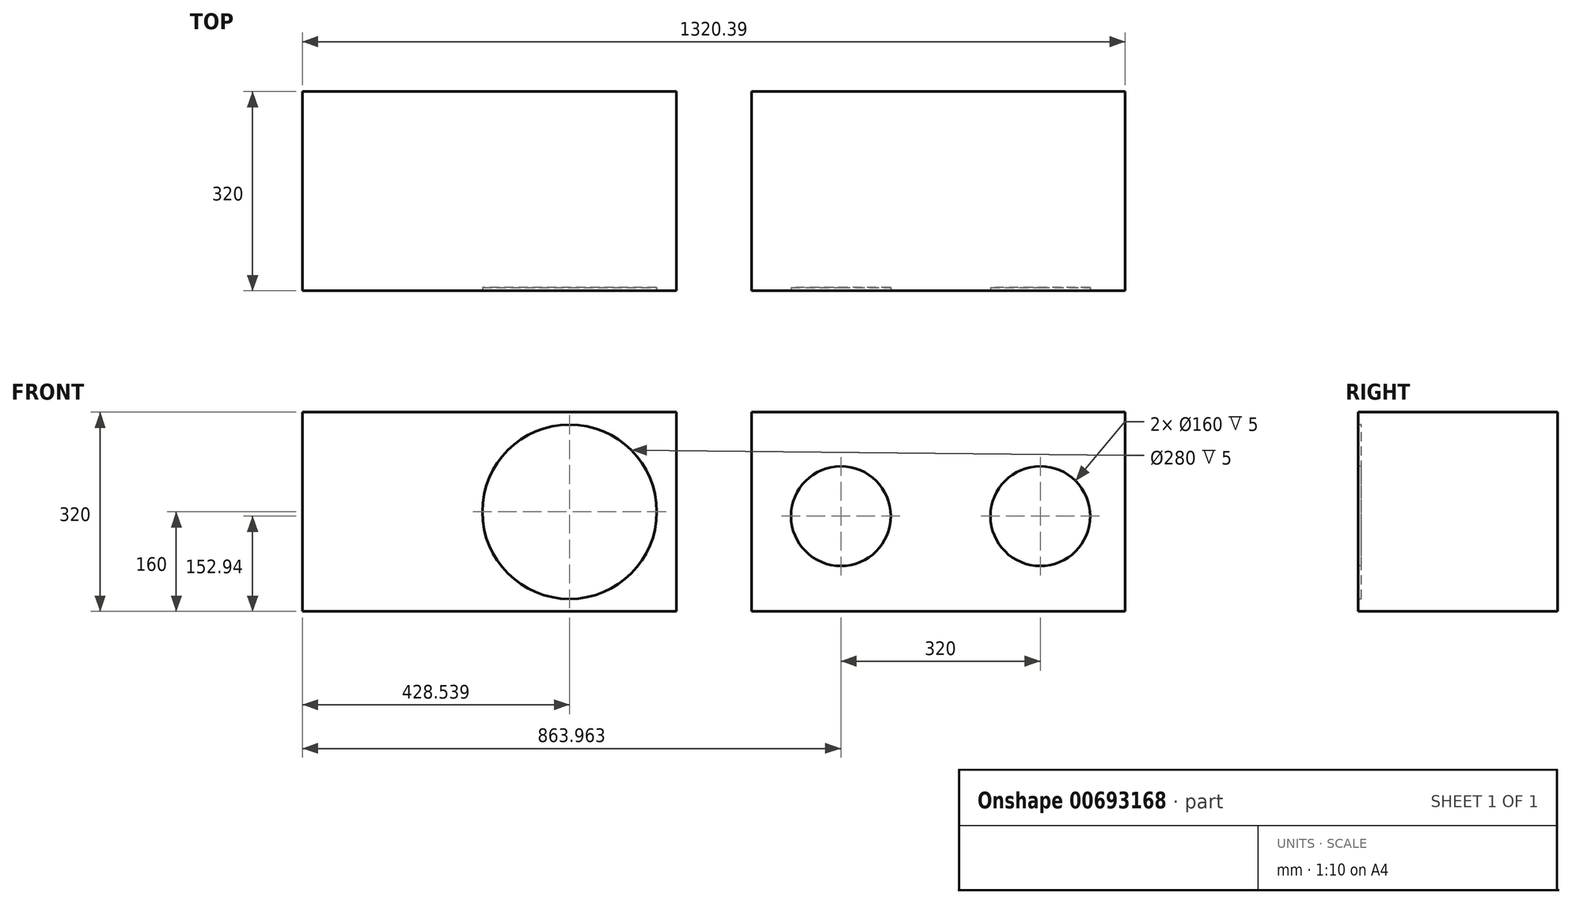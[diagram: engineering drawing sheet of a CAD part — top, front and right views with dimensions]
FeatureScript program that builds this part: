
annotation { "Feature Type Name" : "Feature", "Feature Type Description" : "" }
export const myFeature = defineFeature(function(context is Context, id is Id, definition is map)
    precondition{}
    {
        {
            var Q0;
            Q0=qCreatedBy(makeId("Front.planeOp"),FACE);
            var sketch = newSketch(context, id + "F0", { "sketchPlane" : qUnion([Q0])});
            skLineSegment(sketch, "E0.bottom", {"start": v(-304.82, 167.06) * mm, "end": v(295.18, 167.06) * mm});
            skLineSegment(sketch, "E0.top", {"start": v(-304.82, -152.94) * mm, "end": v(295.18, -152.94) * mm});
            skLineSegment(sketch, "E0.left", {"start": v(-304.82, 167.06) * mm, "end": v(-304.82, -152.94) * mm});
            skLineSegment(sketch, "E0.right", {"start": v(295.18, 167.06) * mm, "end": v(295.18, -152.94) * mm});
            skLineSegment(sketch, "E1.bottom", {"start": v(415.57, 167.06) * mm, "end": v(1015.57, 167.06) * mm});
            skLineSegment(sketch, "E1.top", {"start": v(415.57, -152.94) * mm, "end": v(1015.57, -152.94) * mm});
            skLineSegment(sketch, "E1.left", {"start": v(415.57, 167.06) * mm, "end": v(415.57, -152.94) * mm});
            skLineSegment(sketch, "E1.right", {"start": v(1015.57, 167.06) * mm, "end": v(1015.57, -152.94) * mm});
            skSolve(sketch);
        }
        {
            var Q0;
            Q0 = qSketchRegion(id + "F0", true);
            extrude(context, id + "F1", {"entities" : qUnion([Q0]), "depth" : 320 * mm, "offsetDistance" : 25 * mm});
        }
        {
            var Q0;
            Q0=makeQuery(id+"F1.opExtrude","CAP_FACE",FACE,{"disambiguationData":[OSD([sQuery(id+"F0.wireOp",EDGE,"E0.bottom"),sQuery(id+"F0.wireOp",EDGE,"E0.top"),sQuery(id+"F0.wireOp",EDGE,"E0.left"),sQuery(id+"F0.wireOp",EDGE,"E0.right")])],"isStart":false});
            var sketch = newSketch(context, id + "F2", { "sketchPlane" : qUnion([Q0])});
            skCircle(sketch, "E2", {"center": v(123.72, 7.06) * mm, "radius": 140 * mm});
            skPoint(sketch, "E3.startSnap0", {"position": v(-304.82, 7.06) * mm});
            skPoint(sketch, "E4", {"position": v(295.18, 7.06) * mm});
            skCircle(sketch, "E5", {"center": v(559.14, 0) * mm, "radius": 80 * mm});
            skCircle(sketch, "E6", {"center": v(879.14, 0) * mm, "radius": 80 * mm});
            skLineSegment(sketch, "E7", {"start": v(559.14, 0) * mm, "end": v(879.14, 0) * mm, "construction": true});
            skSolve(sketch);
        }
        {
            var Q0;
            Q0 = qSketchRegion(id + "F2", true);
            extrude(context, id + "F3", {"entities" : qUnion([Q0]), "operationType" : NewBodyOperationType.REMOVE, "oppositeDirection" : true, "depth" : 5 * mm, "offsetDistance" : 25 * mm});
        }
    });
